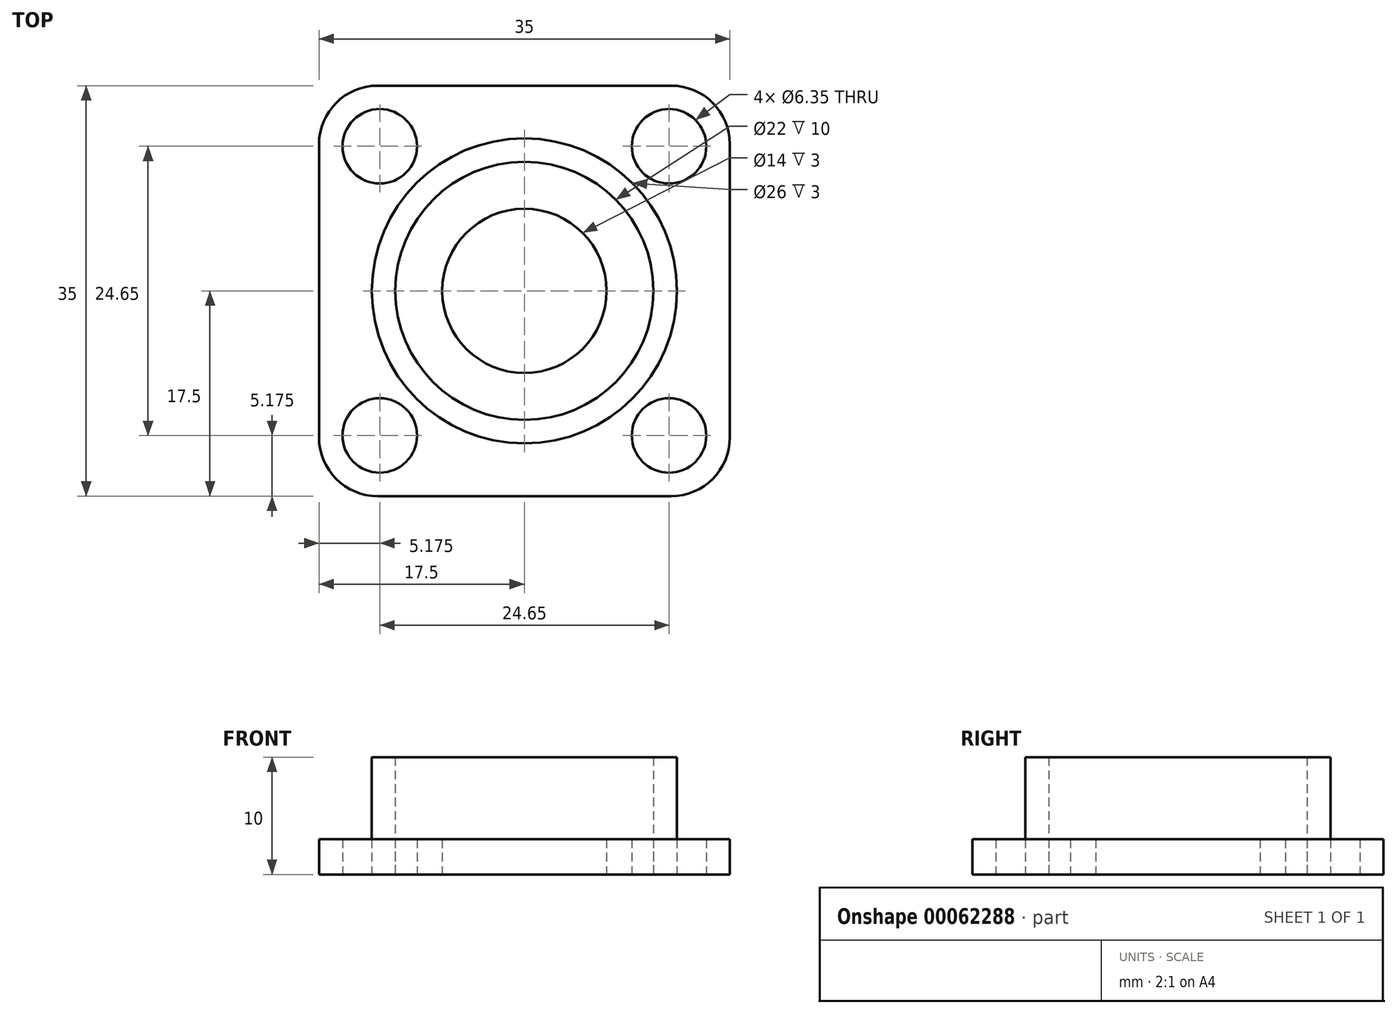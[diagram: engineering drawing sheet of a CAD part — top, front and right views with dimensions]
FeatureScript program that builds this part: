
annotation { "Feature Type Name" : "Feature", "Feature Type Description" : "" }
export const myFeature = defineFeature(function(context is Context, id is Id, definition is map)
    precondition{}
    {
        {
            var Q0;
            Q0=qCreatedBy(makeId("Top.planeOp"),FACE);
            var sketch = newSketch(context, id + "F0", { "sketchPlane" : qUnion([Q0])});
            skCircle(sketch, "E0", {"center": v(0, 0) * mm, "radius": 11 * mm});
            skCircle(sketch, "E1", {"center": v(0, 0) * mm, "radius": 4 * mm, "construction": true});
            skCircle(sketch, "E2.0", {"center": v(0, 0) * mm, "radius": 7 * mm});
            skLineSegment(sketch, "E3.rect.bottom", {"start": v(12.5, 17.5) * mm, "end": v(-12.5, 17.5) * mm});
            skLineSegment(sketch, "E3.rect.top", {"start": v(12.5, -17.5) * mm, "end": v(-12.5, -17.5) * mm});
            skLineSegment(sketch, "E3.rect.left", {"start": v(17.5, 12.5) * mm, "end": v(17.5, -12.5) * mm});
            skLineSegment(sketch, "E3.rect.right", {"start": v(-17.5, 12.5) * mm, "end": v(-17.5, -12.5) * mm});
            skCircle(sketch, "E4.0", {"center": v(0, 0) * mm, "radius": 13 * mm});
            skPoint(sketch, "E5.visualSharp", {"position": v(-17.5, 17.5) * mm});
            skArc(sketch, "E5.filletArc", {"start": v(-12.5, 17.5) * mm, "mid": v(-16.04, 16.04) * mm, "end": v(-17.5, 12.5) * mm});
            skPoint(sketch, "E6.visualSharp", {"position": v(-17.5, -17.5) * mm});
            skArc(sketch, "E6.filletArc", {"start": v(-17.5, -12.5) * mm, "mid": v(-16.04, -16.04) * mm, "end": v(-12.5, -17.5) * mm});
            skPoint(sketch, "E7.visualSharp", {"position": v(17.5, -17.5) * mm});
            skArc(sketch, "E7.filletArc", {"start": v(12.5, -17.5) * mm, "mid": v(16.04, -16.04) * mm, "end": v(17.5, -12.5) * mm});
            skPoint(sketch, "E8.visualSharp", {"position": v(17.5, 17.5) * mm});
            skArc(sketch, "E8.filletArc", {"start": v(17.5, 12.5) * mm, "mid": v(16.04, 16.04) * mm, "end": v(12.5, 17.5) * mm});
            skCircle(sketch, "E9", {"center": v(-12.33, 12.32) * mm, "radius": 3.18 * mm});
            skCircle(sketch, "E10.1.0", {"center": v(-12.32, -12.33) * mm, "radius": 3.18 * mm});
            skCircle(sketch, "E10.2.0", {"center": v(12.32, -12.33) * mm, "radius": 3.18 * mm});
            skCircle(sketch, "E10.3.0", {"center": v(12.32, 12.33) * mm, "radius": 3.18 * mm});
            skSolve(sketch);
        }
        {
            var Q0;
            Q0=makeQuery(id+"F0.imprint","IMPRINT",FACE,{"disambiguationData":[TD([[makeQuery(id+"F0.imprint","IMPRINT",EDGE,{"derivedFrom":sQuery(id+"F0.wireOp",EDGE,"E3.rect.bottom")}),1.0]])]});
            var Q1;
            Q1=makeQuery(id+"F0.imprint","IMPRINT",FACE,{"disambiguationData":[TD([[makeQuery(id+"F0.imprint","IMPRINT",EDGE,{"derivedFrom":sQuery(id+"F0.wireOp",EDGE,"E0")}),1.0]])]});
            extrude(context, id + "F1", {"entities" : qUnion([Q0, Q1]), "depth" : 3 * mm});
        }
        {
            var Q0;
            Q0=makeQuery(id+"F0.imprint","IMPRINT",FACE,{"disambiguationData":[TD([[makeQuery(id+"F0.imprint","IMPRINT",EDGE,{"derivedFrom":sQuery(id+"F0.wireOp",EDGE,"E0")}),-1.0]])]});
            extrude(context, id + "F2", {"entities" : qUnion([Q0]), "depth" : 10 * mm});
        }
    });
